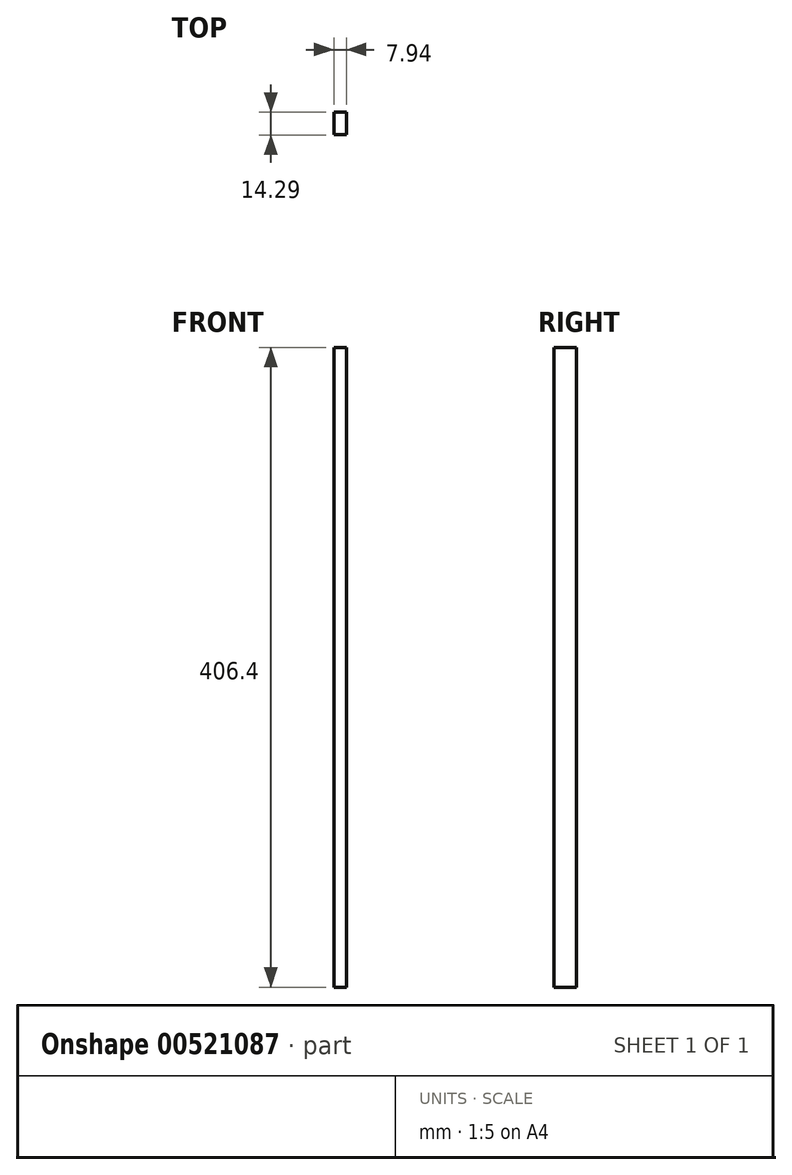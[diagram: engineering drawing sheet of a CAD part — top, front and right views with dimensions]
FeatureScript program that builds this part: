
annotation { "Feature Type Name" : "Feature", "Feature Type Description" : "" }
export const myFeature = defineFeature(function(context is Context, id is Id, definition is map)
    precondition{}
    {
        {
            var Q0;
            Q0=qCreatedBy(makeId("Top.planeOp"),FACE);
            var sketch = newSketch(context, id + "F0", { "sketchPlane" : qUnion([Q0])});
            skLineSegment(sketch, "E0", {"start": v(0, 84.2) * mm, "end": v(0, -97.88) * mm, "construction": true});
            skLineSegment(sketch, "E1", {"start": v(-103.43, 0) * mm, "end": v(103, 0) * mm, "construction": true});
            skLineSegment(sketch, "E2.bottom", {"start": v(-22.22, 57.15) * mm, "end": v(22.22, 57.15) * mm});
            skLineSegment(sketch, "E2.top", {"start": v(-22.22, -57.15) * mm, "end": v(22.23, -57.15) * mm});
            skLineSegment(sketch, "E2.left", {"start": v(-22.22, 57.15) * mm, "end": v(-22.22, -57.15) * mm});
            skLineSegment(sketch, "E2.right", {"start": v(22.23, 57.15) * mm, "end": v(22.23, -57.15) * mm});
            skLineSegment(sketch, "E3", {"start": v(14.29, 57.15) * mm, "end": v(14.29, -57.15) * mm, "construction": true});
            skLineSegment(sketch, "E4.bottom", {"start": v(22.22, 57.15) * mm, "end": v(14.29, 57.15) * mm});
            skLineSegment(sketch, "E4.top", {"start": v(22.23, 42.86) * mm, "end": v(14.29, 42.86) * mm});
            skLineSegment(sketch, "E4.left", {"start": v(22.22, 57.15) * mm, "end": v(22.22, 42.86) * mm});
            skLineSegment(sketch, "E4.right", {"start": v(14.29, 57.15) * mm, "end": v(14.29, 42.86) * mm});
            skLineSegment(sketch, "E5.0.1.0", {"start": v(22.23, 14.29) * mm, "end": v(14.29, 14.29) * mm});
            skLineSegment(sketch, "E5.0.1.1", {"start": v(14.29, 28.58) * mm, "end": v(14.29, 14.29) * mm});
            skLineSegment(sketch, "E5.0.1.2", {"start": v(22.22, 28.58) * mm, "end": v(14.29, 28.58) * mm});
            skLineSegment(sketch, "E5.0.2.0", {"start": v(22.23, -14.29) * mm, "end": v(14.29, -14.29) * mm});
            skLineSegment(sketch, "E5.0.2.1", {"start": v(14.29, 0) * mm, "end": v(14.29, -14.29) * mm});
            skLineSegment(sketch, "E5.0.2.2", {"start": v(22.22, 0) * mm, "end": v(14.29, 0) * mm});
            skLineSegment(sketch, "E5.0.3.0", {"start": v(22.23, -42.86) * mm, "end": v(14.29, -42.86) * mm});
            skLineSegment(sketch, "E5.0.3.1", {"start": v(14.29, -28.58) * mm, "end": v(14.29, -42.86) * mm});
            skLineSegment(sketch, "E5.0.3.2", {"start": v(22.22, -28.58) * mm, "end": v(14.29, -28.58) * mm});
            skLineSegment(sketch, "E5.direction1", {"start": v(14.29, 42.86) * mm, "end": v(39.69, 42.86) * mm, "construction": true});
            skLineSegment(sketch, "E5.direction2", {"start": v(14.29, 42.86) * mm, "end": v(14.29, 14.29) * mm, "construction": true});
            skSolve(sketch);
        }
        {
            var Q0;
            Q0=makeQuery(id+"F0.imprint","IMPRINT",FACE,{"disambiguationData":[TD([[makeQuery(id+"F0.imprint","IMPRINT",EDGE,{"derivedFrom":sQuery(id+"F0.wireOp",EDGE,"E2.bottom")}),-1.0]])]});
            extrude(context, id + "F1", {"entities" : qUnion([Q0]), "endBound" : BoundingType.SYMMETRIC, "depth" : 406.4 * mm, "offsetDistance" : 25.4 * mm});
        }
        {
            var Q0;
            {var subQ0=sQuery(id+"F0.wireOp",EDGE,"E2.right");Q0=makeQuery(id+"F1.opExtrude","SWEPT_FACE",FACE,{"disambiguationData":[OSD([subQ0]),TDD([makeQuery(id+"F0.imprint","IMPRINT",EDGE,{"disambiguationData":[TD([[makeQuery(id+"F0.imprint","INTERSECT",VERTEX,{"derivedFrom":[subQ0,sQuery(id+"F0.wireOp",EDGE,"E5.0.1.0")]}),-1.0]])],"derivedFrom":subQ0})])]});}
            var sketch = newSketch(context, id + "F2", { "sketchPlane" : qUnion([Q0])});
            skCircle(sketch, "E6", {"center": v(7.14, 57.15) * mm, "radius": 5.56 * mm});
            skCircle(sketch, "E7", {"center": v(7.14, 88.9) * mm, "radius": 5.56 * mm});
            skLineSegment(sketch, "E8.0.0", {"start": v(-28.58, -203.2) * mm, "end": v(-14.29, -203.2) * mm});
            skLineSegment(sketch, "E8.0.1", {"start": v(-14.29, -203.2) * mm, "end": v(-14.29, 203.2) * mm});
            skLineSegment(sketch, "E8.0.2", {"start": v(-14.29, 203.2) * mm, "end": v(-28.58, 203.2) * mm});
            skLineSegment(sketch, "E8.0.3", {"start": v(-28.58, 203.2) * mm, "end": v(-28.58, -203.2) * mm});
            skLineSegment(sketch, "E9.0.0", {"start": v(0, -203.2) * mm, "end": v(14.29, -203.2) * mm});
            skLineSegment(sketch, "E9.0.1", {"start": v(14.29, -203.2) * mm, "end": v(14.29, 203.2) * mm});
            skLineSegment(sketch, "E9.0.2", {"start": v(14.29, 203.2) * mm, "end": v(0, 203.2) * mm});
            skLineSegment(sketch, "E9.0.3", {"start": v(0, 203.2) * mm, "end": v(0, -203.2) * mm});
            skLineSegment(sketch, "E10", {"start": v(7.14, 203.2) * mm, "end": v(7.14, -203.2) * mm, "construction": true});
            skSolve(sketch);
        }
        {
            var Q0;
            Q0=makeQuery(id+"F2.imprint","IMPRINT",FACE,{"disambiguationData":[TD([[makeQuery(id+"F2.imprint","IMPRINT",EDGE,{"derivedFrom":sQuery(id+"F2.wireOp",EDGE,"E7")}),1.0]])]});
            var Q1;
            Q1=makeQuery(id+"F2.imprint","IMPRINT",FACE,{"disambiguationData":[TD([[makeQuery(id+"F2.imprint","IMPRINT",EDGE,{"derivedFrom":sQuery(id+"F2.wireOp",EDGE,"E6")}),1.0]])]});
            extrude(context, id + "F3", {"entities" : qUnion([Q0, Q1]), "operationType" : NewBodyOperationType.REMOVE, "endBound" : BoundingType.THROUGH_ALL, "oppositeDirection" : true, "depth" : 25.4 * mm, "offsetDistance" : 25.4 * mm});
        }
        {
            var Q0;
            Q0=makeQuery(id+"F1.opExtrude","CAP_FACE",FACE,{"disambiguationData":[OSD([sQuery(id+"F0.wireOp",EDGE,"E2.bottom"),sQuery(id+"F0.wireOp",EDGE,"E2.top"),sQuery(id+"F0.wireOp",EDGE,"E2.left"),sQuery(id+"F0.wireOp",EDGE,"E2.right"),sQuery(id+"F0.wireOp",EDGE,"E4.top"),sQuery(id+"F0.wireOp",EDGE,"E4.right"),sQuery(id+"F0.wireOp",EDGE,"E5.0.1.0"),sQuery(id+"F0.wireOp",EDGE,"E5.0.1.1"),sQuery(id+"F0.wireOp",EDGE,"E5.0.1.2"),sQuery(id+"F0.wireOp",EDGE,"E5.0.2.0"),sQuery(id+"F0.wireOp",EDGE,"E5.0.2.1"),sQuery(id+"F0.wireOp",EDGE,"E5.0.2.2"),sQuery(id+"F0.wireOp",EDGE,"E5.0.3.0"),sQuery(id+"F0.wireOp",EDGE,"E5.0.3.1"),sQuery(id+"F0.wireOp",EDGE,"E5.0.3.2")])],"isStart":true});
            var sketch = newSketch(context, id + "F4", { "sketchPlane" : qUnion([Q0])});
            skLineSegment(sketch, "E11", {"start": v(-3.17, 57.15) * mm, "end": v(-3.17, -57.15) * mm, "construction": true});
            skPoint(sketch, "E11.endSnap0", {"position": v(-3.97, -57.15) * mm});
            skCircle(sketch, "E12", {"center": v(-3.17, 38.1) * mm, "radius": 9.53 * mm});
            skCircle(sketch, "E13", {"center": v(-3.17, -38.1) * mm, "radius": 9.53 * mm});
            skLineSegment(sketch, "E14", {"start": v(-44.01, 0) * mm, "end": v(44.7, 0) * mm, "construction": true});
            skSolve(sketch);
        }
        {
            var Q0;
            Q0 = qSketchRegion(id + "F4", true);
            extrude(context, id + "F5", {"entities" : qUnion([Q0]), "operationType" : NewBodyOperationType.REMOVE, "oppositeDirection" : true, "depth" : 76.2 * mm, "offsetDistance" : 25.4 * mm});
        }
    });
